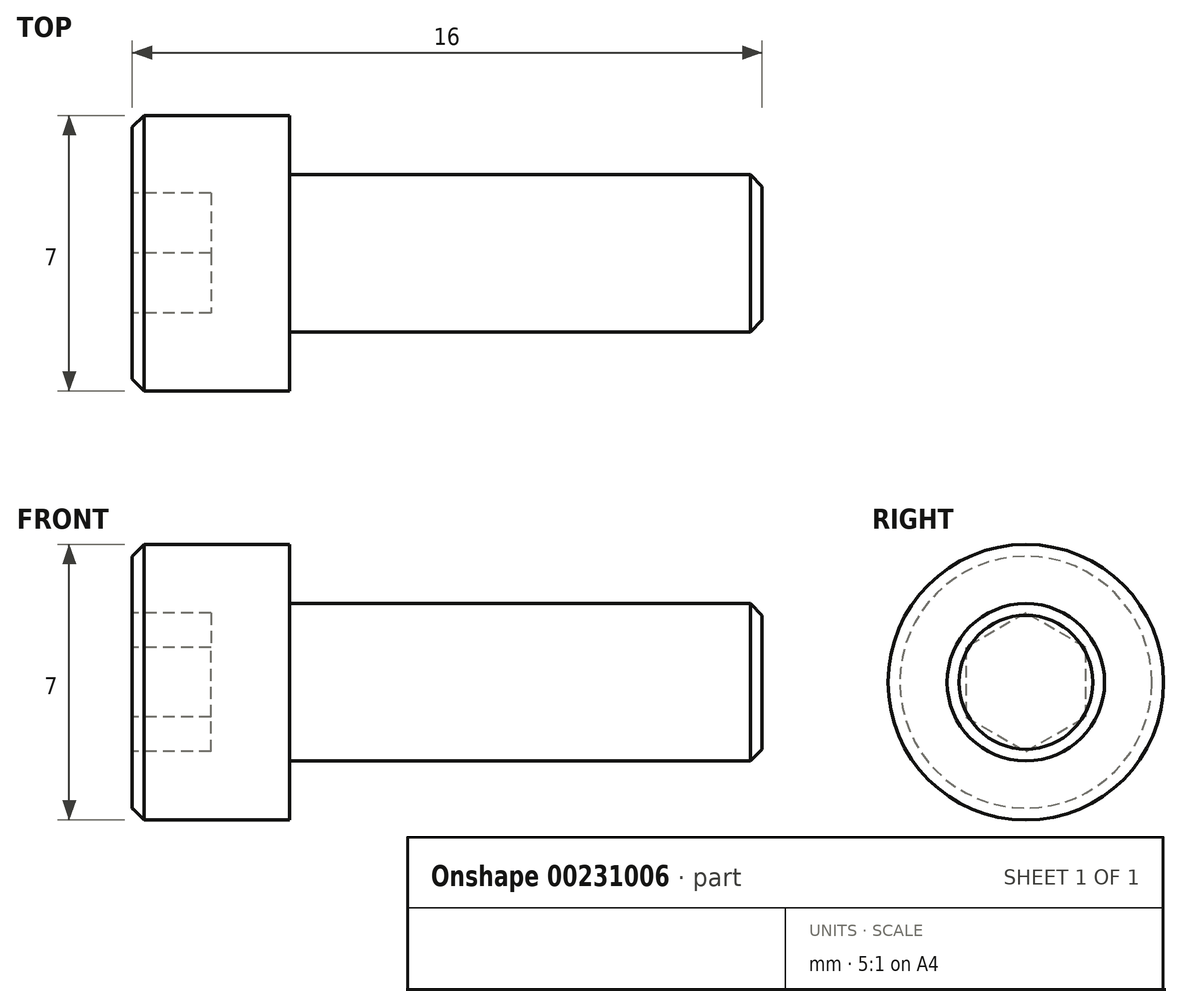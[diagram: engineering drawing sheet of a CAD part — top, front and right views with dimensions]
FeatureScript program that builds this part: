
annotation { "Feature Type Name" : "Feature", "Feature Type Description" : "" }
export const myFeature = defineFeature(function(context is Context, id is Id, definition is map)
    precondition{}
    {
        {
            var Q0;
            Q0=qCreatedBy(makeId("Top.planeOp"),FACE);
            var sketch = newSketch(context, id + "F0", { "sketchPlane" : qUnion([Q0])});
            skLineSegment(sketch, "E0", {"start": v(0, 0) * mm, "end": v(10.82, 0) * mm, "construction": true});
            skLineSegment(sketch, "E1", {"start": v(0, 0) * mm, "end": v(0, 3.5) * mm});
            skLineSegment(sketch, "E2", {"start": v(0, 3.5) * mm, "end": v(4, 3.5) * mm});
            skLineSegment(sketch, "E3", {"start": v(4, 3.5) * mm, "end": v(4, 2) * mm});
            skLineSegment(sketch, "E4", {"start": v(4, 2) * mm, "end": v(16, 2) * mm});
            skLineSegment(sketch, "E5", {"start": v(16, 2) * mm, "end": v(16, 0) * mm});
            skLineSegment(sketch, "E6", {"start": v(16, 0) * mm, "end": v(0, 0) * mm});
            skSolve(sketch);
        }
        {
            var Q0;
            Q0=makeQuery(id+"F0.imprint","IMPRINT",FACE,{"disambiguationData":[TD([[makeQuery(id+"F0.imprint","IMPRINT",EDGE,{"derivedFrom":sQuery(id+"F0.wireOp",EDGE,"E1")}),-1.0]])]});
            var Q1;
            Q1=sQuery(id+"F0.wireOp",EDGE,"E6");
            revolve(context, id + "F1", {"entities" : qUnion([Q0]), "axis" : qUnion([Q1]), "revolveType" : RevolveType.FULL});
        }
        {
            var Q0;
            Q0=makeQuery(id+"F1.opRevolve","SWEPT_EDGE",EDGE,{"disambiguationData":[OSD([sQuery(id+"F0.wireOp",EDGE,"E1"),sQuery(id+"F0.wireOp",EDGE,"E2")])]});
            var Q1;
            Q1=makeQuery(id+"F1.opRevolve","SWEPT_EDGE",EDGE,{"disambiguationData":[OSD([sQuery(id+"F0.wireOp",EDGE,"E4"),sQuery(id+"F0.wireOp",EDGE,"E5")])]});
            chamfer(context, id + "F2", {"entities" : qUnion([Q0, Q1]), "width" : 0.3 * mm, "tangentPropagation" : true});
        }
        {
            var Q0;
            Q0=makeQuery(id+"F1.opRevolve","SWEPT_FACE",FACE,{"disambiguationData":[OSD([sQuery(id+"F0.wireOp",EDGE,"E1")])]});
            var sketch = newSketch(context, id + "F3", { "sketchPlane" : qUnion([Q0])});
            skCircle(sketch, "E7.cCircle", {"center": v(0, 0) * mm, "radius": 1.76 * mm, "construction": true});
            skLineSegment(sketch, "E7.0", {"start": v(0, 1.76) * mm, "end": v(1.52, 0.88) * mm});
            skLineSegment(sketch, "E7.1", {"start": v(1.52, 0.88) * mm, "end": v(1.52, -0.88) * mm});
            skLineSegment(sketch, "E7.2", {"start": v(1.52, -0.88) * mm, "end": v(0, -1.76) * mm});
            skLineSegment(sketch, "E7.3", {"start": v(0, -1.76) * mm, "end": v(-1.52, -0.88) * mm});
            skLineSegment(sketch, "E7.4", {"start": v(-1.52, -0.88) * mm, "end": v(-1.53, 0.88) * mm});
            skLineSegment(sketch, "E7.5", {"start": v(-1.53, 0.88) * mm, "end": v(0, 1.76) * mm});
            skSolve(sketch);
        }
        {
            var Q0;
            Q0=makeQuery(id+"F3.imprint","IMPRINT",FACE,{"disambiguationData":[TD([[makeQuery(id+"F3.imprint","IMPRINT",EDGE,{"derivedFrom":sQuery(id+"F3.wireOp",EDGE,"E7.0")}),-1.0]])]});
            extrude(context, id + "F4", {"entities" : qUnion([Q0]), "operationType" : NewBodyOperationType.REMOVE, "oppositeDirection" : true, "depth" : 2 * mm});
        }
    });
